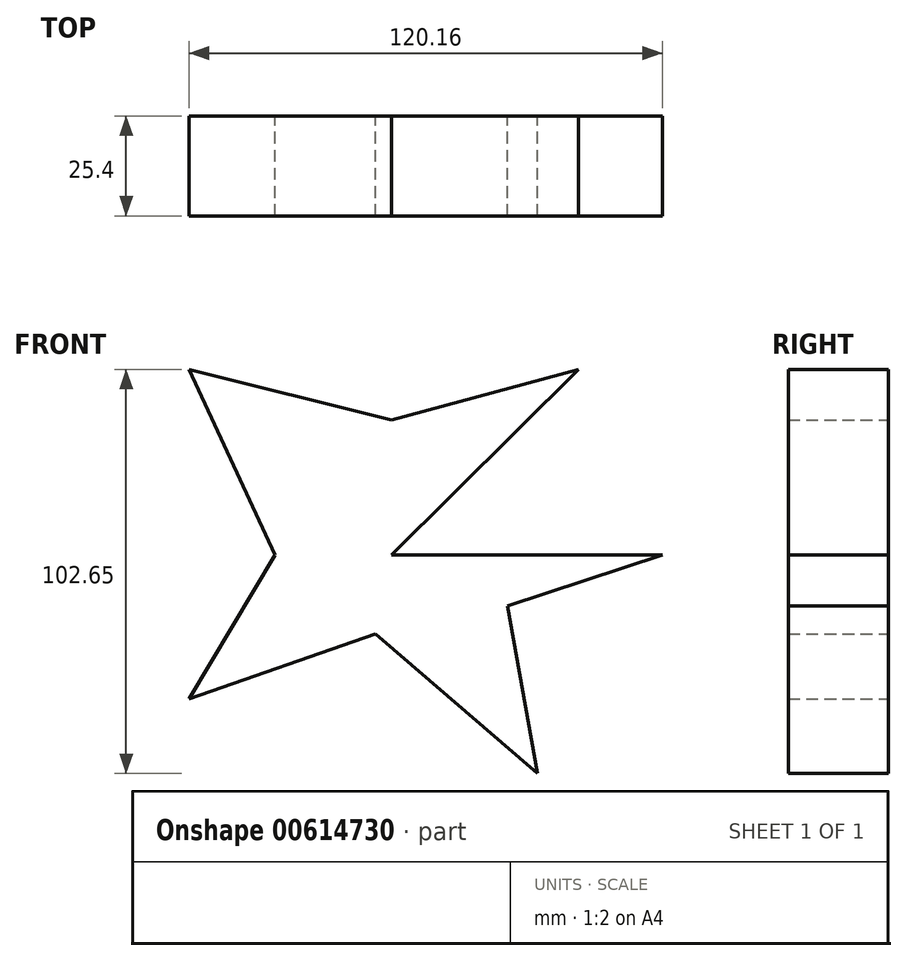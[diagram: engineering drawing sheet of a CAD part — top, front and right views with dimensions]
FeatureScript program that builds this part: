
annotation { "Feature Type Name" : "Feature", "Feature Type Description" : "" }
export const myFeature = defineFeature(function(context is Context, id is Id, definition is map)
    precondition{}
    {
        {
            var Q0;
            Q0=qCreatedBy(makeId("Front.planeOp"),FACE);
            var sketch = newSketch(context, id + "F0", { "sketchPlane" : qUnion([Q0])});
            skLineSegment(sketch, "E0", {"start": v(0, 0) * mm, "end": v(47.54, 47.07) * mm});
            skLineSegment(sketch, "E1", {"start": v(47.54, 47.07) * mm, "end": v(0, 34.3) * mm});
            skLineSegment(sketch, "E2", {"start": v(0, 34.3) * mm, "end": v(-51.33, 47.07) * mm});
            skLineSegment(sketch, "E3", {"start": v(-51.33, 47.07) * mm, "end": v(-29.57, 0) * mm});
            skLineSegment(sketch, "E4", {"start": v(-29.57, 0) * mm, "end": v(-51.33, -36.66) * mm});
            skLineSegment(sketch, "E5", {"start": v(-51.33, -36.66) * mm, "end": v(-4.02, -20.1) * mm});
            skLineSegment(sketch, "E6", {"start": v(-4.02, -20.1) * mm, "end": v(37.13, -55.58) * mm});
            skLineSegment(sketch, "E7", {"start": v(37.13, -55.58) * mm, "end": v(29.57, -13) * mm});
            skLineSegment(sketch, "E8", {"start": v(29.57, -13) * mm, "end": v(68.83, 0) * mm});
            skLineSegment(sketch, "E9", {"start": v(68.83, 0) * mm, "end": v(0, 0) * mm});
            skSolve(sketch);
        }
        {
            var Q0;
            Q0 = qSketchRegion(id + "F0", true);
            extrude(context, id + "F1", {"entities" : qUnion([Q0]), "depth" : 25.4 * mm, "offsetDistance" : 25.4 * mm});
        }
    });
